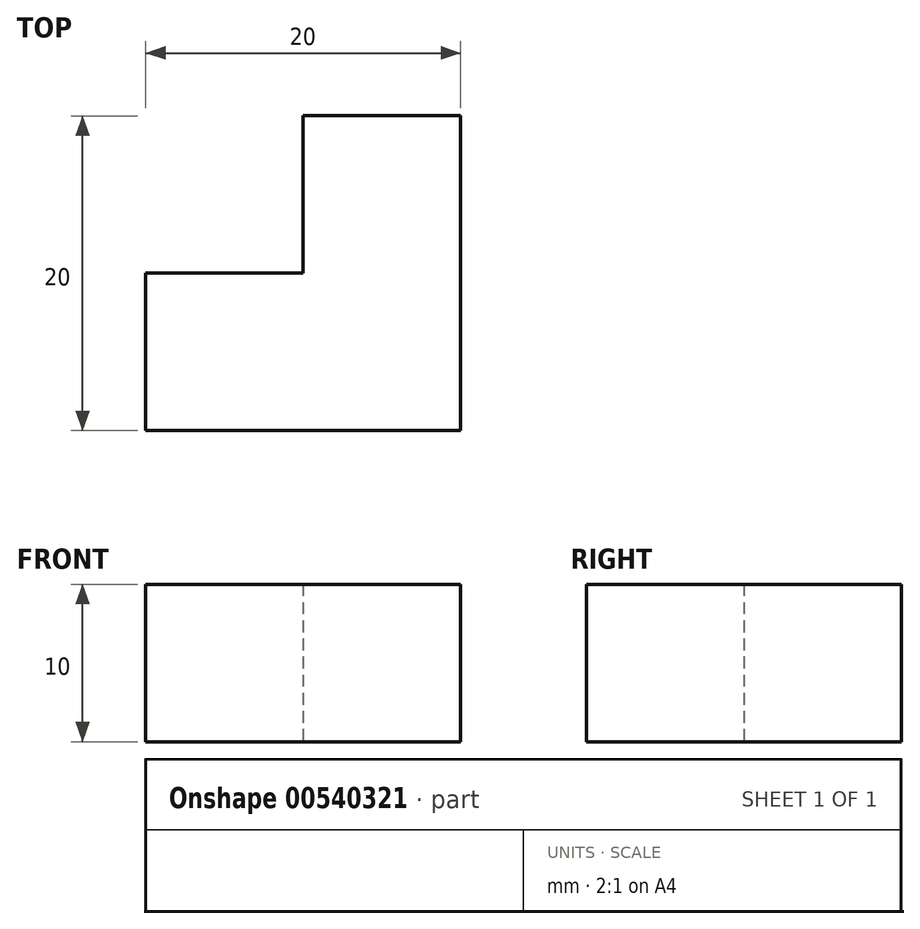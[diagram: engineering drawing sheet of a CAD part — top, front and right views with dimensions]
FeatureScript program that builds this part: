
annotation { "Feature Type Name" : "Feature", "Feature Type Description" : "" }
export const myFeature = defineFeature(function(context is Context, id is Id, definition is map)
    precondition{}
    {
        {
            var Q0;
            Q0=qCreatedBy(makeId("Top.planeOp"),FACE);
            var sketch = newSketch(context, id + "F0", { "sketchPlane" : qUnion([Q0])});
            skLineSegment(sketch, "E0", {"start": v(-47.7, 2.21) * mm, "end": v(-47.7, -17.79) * mm});
            skLineSegment(sketch, "E1", {"start": v(-47.7, -17.79) * mm, "end": v(-67.7, -17.79) * mm});
            skLineSegment(sketch, "E2", {"start": v(-67.7, -17.79) * mm, "end": v(-67.7, -7.79) * mm});
            skLineSegment(sketch, "E3", {"start": v(-67.7, -7.79) * mm, "end": v(-57.7, -7.79) * mm});
            skLineSegment(sketch, "E4", {"start": v(-57.7, -7.79) * mm, "end": v(-57.7, 2.21) * mm});
            skLineSegment(sketch, "E5", {"start": v(-57.7, 2.21) * mm, "end": v(-47.7, 2.21) * mm});
            skSolve(sketch);
        }
        {
            var Q0;
            Q0=makeQuery(id+"F0.imprint","IMPRINT",FACE,{"disambiguationData":[TD([[makeQuery(id+"F0.imprint","IMPRINT",EDGE,{"derivedFrom":sQuery(id+"F0.wireOp",EDGE,"E0")}),-1.0]])]});
            extrude(context, id + "F1", {"entities" : qUnion([Q0]), "depth" : 10 * mm, "offsetDistance" : 25 * mm});
        }
    });
